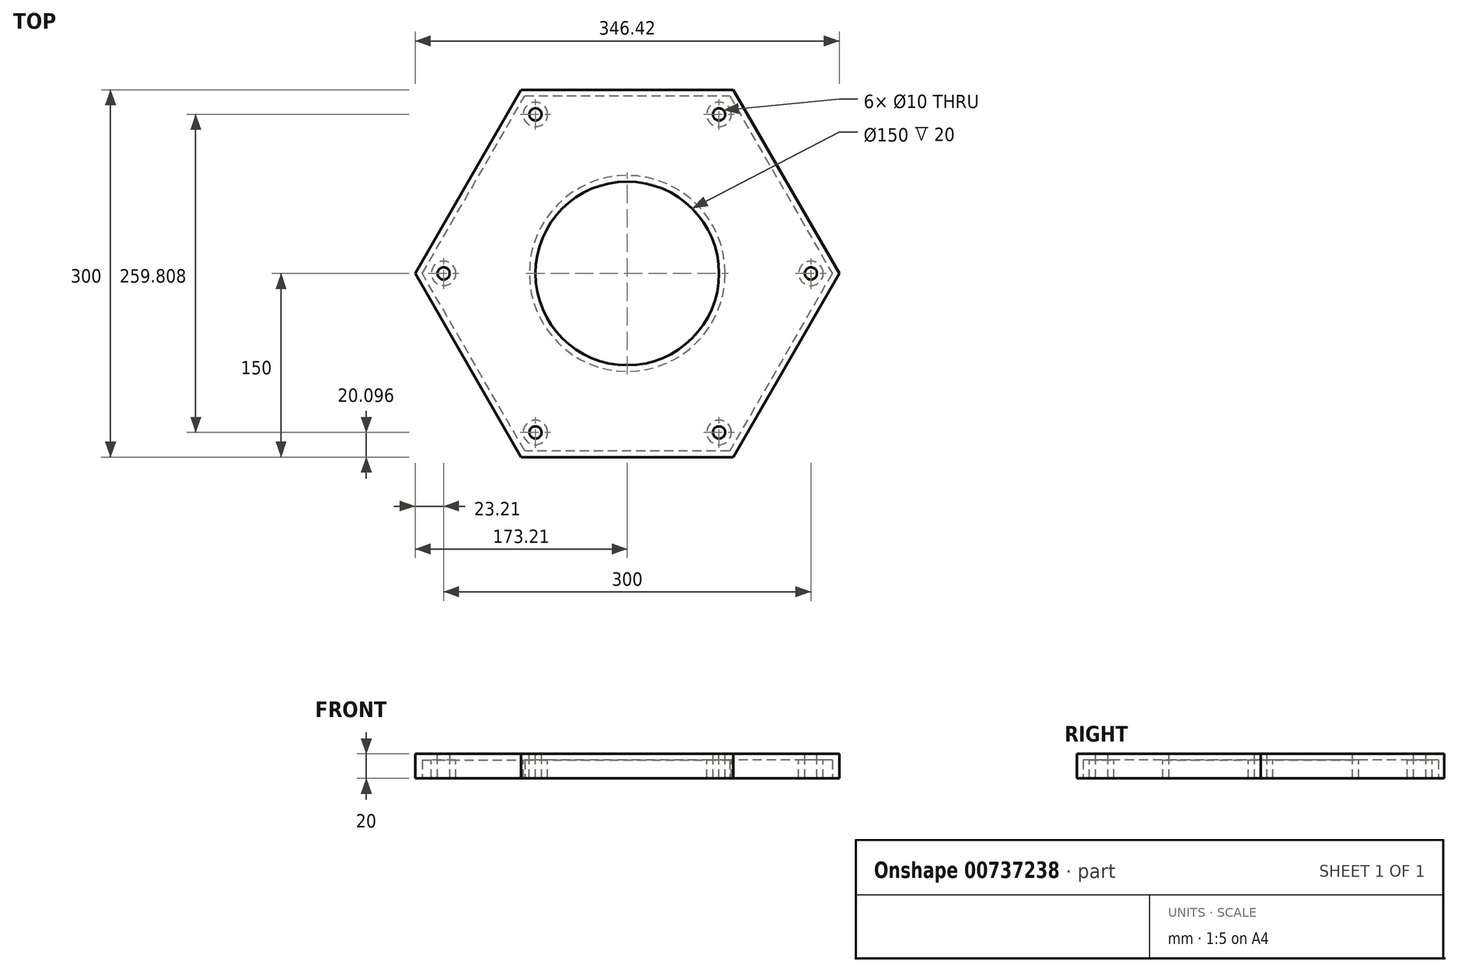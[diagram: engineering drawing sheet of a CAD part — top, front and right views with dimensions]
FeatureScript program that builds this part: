
annotation { "Feature Type Name" : "Feature", "Feature Type Description" : "" }
export const myFeature = defineFeature(function(context is Context, id is Id, definition is map)
    precondition{}
    {
        {
            var Q0;
            Q0=qCreatedBy(makeId("Top.planeOp"),FACE);
            var sketch = newSketch(context, id + "F0", { "sketchPlane" : qUnion([Q0])});
            skCircle(sketch, "E0.cCircle", {"center": v(0, 0) * mm, "radius": 150 * mm, "construction": true});
            skLineSegment(sketch, "E0.0", {"start": v(173.2, 0) * mm, "end": v(86.6, -150) * mm});
            skLineSegment(sketch, "E0.1", {"start": v(86.6, -150) * mm, "end": v(-86.6, -150) * mm});
            skLineSegment(sketch, "E0.2", {"start": v(-86.6, -150) * mm, "end": v(-173.2, 0) * mm});
            skLineSegment(sketch, "E0.3", {"start": v(-173.2, 0) * mm, "end": v(-86.6, 150) * mm});
            skLineSegment(sketch, "E0.4", {"start": v(-86.6, 150) * mm, "end": v(86.6, 150) * mm});
            skLineSegment(sketch, "E0.5", {"start": v(86.6, 150) * mm, "end": v(173.2, 0) * mm});
            skPoint(sketch, "E0.0.midPoint", {"position": v(129.9, -75) * mm});
            skSolve(sketch);
        }
        {
            var Q0;
            Q0=makeQuery(id+"F0.imprint","IMPRINT",FACE,{"disambiguationData":[TD([[makeQuery(id+"F0.imprint","IMPRINT",EDGE,{"derivedFrom":sQuery(id+"F0.wireOp",EDGE,"E0.0")}),-1.0]])]});
            extrude(context, id + "F1", {"entities" : qUnion([Q0]), "depth" : 20 * mm, "offsetDistance" : 25 * mm});
        }
        {
            var Q0;
            Q0=makeQuery(id+"F1.opExtrude","CAP_FACE",FACE,{"disambiguationData":[OSD([sQuery(id+"F0.wireOp",EDGE,"E0.0"),sQuery(id+"F0.wireOp",EDGE,"E0.1"),sQuery(id+"F0.wireOp",EDGE,"E0.2"),sQuery(id+"F0.wireOp",EDGE,"E0.3"),sQuery(id+"F0.wireOp",EDGE,"E0.4"),sQuery(id+"F0.wireOp",EDGE,"E0.5")])],"isStart":false});
            var sketch = newSketch(context, id + "F2", { "sketchPlane" : qUnion([Q0])});
            skCircle(sketch, "E1", {"center": v(0, 0) * mm, "radius": 75 * mm});
            skSolve(sketch);
        }
        {
            var Q0;
            Q0 = qSketchRegion(id + "F2", true);
            extrude(context, id + "F3", {"entities" : qUnion([Q0]), "operationType" : NewBodyOperationType.REMOVE, "endBound" : BoundingType.THROUGH_ALL, "oppositeDirection" : true, "depth" : 25 * mm, "offsetDistance" : 25 * mm});
        }
        {
            var Q0;
            Q0=makeQuery(id+"F1.opExtrude","CAP_FACE",FACE,{"disambiguationData":[OSD([sQuery(id+"F0.wireOp",EDGE,"E0.0"),sQuery(id+"F0.wireOp",EDGE,"E0.1"),sQuery(id+"F0.wireOp",EDGE,"E0.2"),sQuery(id+"F0.wireOp",EDGE,"E0.3"),sQuery(id+"F0.wireOp",EDGE,"E0.4"),sQuery(id+"F0.wireOp",EDGE,"E0.5")])],"isStart":false});
            var sketch = newSketch(context, id + "F4", { "sketchPlane" : qUnion([Q0])});
            skCircle(sketch, "E2", {"center": v(-75, 129.9) * mm, "radius": 5 * mm});
            skLineSegment(sketch, "E3", {"start": v(0, 0) * mm, "end": v(-86.6, 150) * mm, "construction": true});
            skLineSegment(sketch, "E4", {"start": v(0, 0) * mm, "end": v(86.6, 150) * mm, "construction": true});
            skLineSegment(sketch, "E5", {"start": v(0, 0) * mm, "end": v(-173.2, 0) * mm, "construction": true});
            skLineSegment(sketch, "E6", {"start": v(0, 0) * mm, "end": v(-86.6, -150) * mm, "construction": true});
            skLineSegment(sketch, "E7", {"start": v(0, 0) * mm, "end": v(173.2, 0) * mm, "construction": true});
            skLineSegment(sketch, "E8", {"start": v(0, 0) * mm, "end": v(86.6, -150) * mm, "construction": true});
            skCircle(sketch, "E9", {"center": v(75, 129.9) * mm, "radius": 5 * mm});
            skCircle(sketch, "E10.1.0", {"center": v(-75, -129.9) * mm, "radius": 5 * mm});
            skCircle(sketch, "E10.1.1", {"center": v(-150, 0) * mm, "radius": 5 * mm});
            skCircle(sketch, "E10.2.0", {"center": v(150, 0) * mm, "radius": 5 * mm});
            skCircle(sketch, "E10.2.1", {"center": v(75, -129.9) * mm, "radius": 5 * mm});
            skPoint(sketch, "E10.center", {"position": v(0, 0) * mm});
            skSolve(sketch);
        }
        {
            var Q0;
            Q0=makeQuery(id+"F4.imprint","IMPRINT",FACE,{"disambiguationData":[TD([[makeQuery(id+"F4.imprint","IMPRINT",EDGE,{"derivedFrom":sQuery(id+"F4.wireOp",EDGE,"E9")}),1.0]])]});
            var Q1;
            Q1=makeQuery(id+"F4.imprint","IMPRINT",FACE,{"disambiguationData":[TD([[makeQuery(id+"F4.imprint","IMPRINT",EDGE,{"derivedFrom":sQuery(id+"F4.wireOp",EDGE,"E10.1.0")}),1.0]])]});
            var Q2;
            Q2=makeQuery(id+"F4.imprint","IMPRINT",FACE,{"disambiguationData":[TD([[makeQuery(id+"F4.imprint","IMPRINT",EDGE,{"derivedFrom":sQuery(id+"F4.wireOp",EDGE,"E10.1.1")}),1.0]])]});
            var Q3;
            Q3=makeQuery(id+"F4.imprint","IMPRINT",FACE,{"disambiguationData":[TD([[makeQuery(id+"F4.imprint","IMPRINT",EDGE,{"derivedFrom":sQuery(id+"F4.wireOp",EDGE,"E10.2.0")}),1.0]])]});
            var Q4;
            Q4=makeQuery(id+"F4.imprint","IMPRINT",FACE,{"disambiguationData":[TD([[makeQuery(id+"F4.imprint","IMPRINT",EDGE,{"derivedFrom":sQuery(id+"F4.wireOp",EDGE,"E10.2.1")}),1.0]])]});
            extrude(context, id + "F5", {"entities" : qUnion([Q0, Q1, Q2, Q3, Q4]), "operationType" : NewBodyOperationType.REMOVE, "endBound" : BoundingType.THROUGH_ALL, "oppositeDirection" : true, "depth" : 25 * mm, "offsetDistance" : 25 * mm});
        }
        {
            var Q0;
            Q0 = qSketchRegion(id + "F4", true);
            extrude(context, id + "F6", {"entities" : qUnion([Q0]), "operationType" : NewBodyOperationType.REMOVE, "oppositeDirection" : true, "depth" : 25 * mm, "offsetDistance" : 25 * mm});
        }
        {
            var Q0;
            Q0=makeQuery(id+"F1.opExtrude","CAP_FACE",FACE,{"disambiguationData":[OSD([sQuery(id+"F0.wireOp",EDGE,"E0.0"),sQuery(id+"F0.wireOp",EDGE,"E0.1"),sQuery(id+"F0.wireOp",EDGE,"E0.2"),sQuery(id+"F0.wireOp",EDGE,"E0.3"),sQuery(id+"F0.wireOp",EDGE,"E0.4"),sQuery(id+"F0.wireOp",EDGE,"E0.5")])],"isStart":true});
            shell(context, id + "F7", {"entities" : qUnion([Q0]), "thickness" : 5 * mm});
        }
    });
